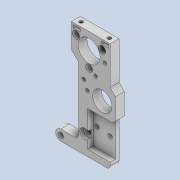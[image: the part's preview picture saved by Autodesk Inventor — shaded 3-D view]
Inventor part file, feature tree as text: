
AUTODESK INVENTOR PART (.ipt)
format: ipt  version: 2020.4 (Build 244396000, 396)  size: 391,168 bytes
history: native  units: mm
features: extrude x7, sketch x6, fillet x2, thread x2, projected_geometry x2
ambient origin geometry x8: Origin, YZ Plane, XZ Plane, XY Plane, X Axis, Y Axis, Z Axis, Center Point
bodies: Solid1 (feature_tree)
feature tree (19):
  extrude  "Extrusion1"  Depth=6.0mm
  fillet  "Fillet1"  Radius=28.0mm
  fillet  "Fillet2"  Radius=6.0mm
  extrude  "Extrusion2"  Depth=3.0mm
  extrude  "Extrusion3"  Depth=56.0mm
  thread  "Thread1"  [1 undecoded]
  thread  "Thread2"  [1 undecoded]
  extrude  "Extrusion4"  Depth=12.5mm
  extrude  "Extrusion5"  Depth=2.1mm
  extrude  "Extrusion6"  Depth=1.8mm TaperAngle=360.0deg
  extrude  "Extrusion7"  Depth=4.0mm
  sketch  "Sketch1"  dims[d0=3.0mm d1=6.0mm d2=28.0mm d3=6.0mm]
  sketch  "Sketch3"  dims[d4=0.0mm d5=3.0mm]
  projected_geometry  "Projected Loop1"
  sketch  "Sketch5"  dims[d6=18.0mm d7=56.0mm d8=11.0mm d9=4.5mm]
  sketch  "Sketch7"  dims[d10=25.5mm d11=12.5mm]
  sketch  "Sketch8"  dims[d12=22.3mm d14=2.1mm]
  projected_geometry  "Projected Loop2"
  sketch  "Sketch10"  dims[d17=9.5mm d18=30.0mm d20=360.0deg d22=4.0mm d23=14.0mm d24=45.0deg d25=3.0mm d26=12.0mm d27=6.0mm d28=135.0deg d29=135.0deg d30=5.0mm d31=0.0mm d32=3.0mm d33=10.5mm d34=3.5mm d35=2.5mm d36=14.5mm d37=7.5mm d38=2.5mm d39=15.0mm d40=13.5mm d41=2.0mm d42=2.0mm d43=12.75mm d44=20.0mm d45=23.75mm d46=3.0mm d47=0.0mm d48=2.0mm d49=2.0mm d50=2.5mm d51=2.5mm d52=3.0mm d53=3.0mm d54=3.0mm d55=0.0mm d56=7.0mm d57=0.0mm d58=7.0mm d59=0.0mm d60=8.5mm d61=270.0deg d62=4.0mm d63=4.0mm d64=4.0mm d65=3.0mm d66=0.0mm d67=5.5mm d68=2.0mm d69=0.0mm d70=4.0mm d71=1.85mm d72=4.0mm d73=1.85mm d74=1.0mm d75=1.8mm d76=1.8mm d77=1.0mm d78=10.0mm d79=0.0mm d82=2.0mm d83=11.15mm d84=2.1mm d85=2.1mm d86=2.1mm d87=5.0mm d88=3.0mm d89=25.0mm d90=29.5mm d91=3.0mm d92=11.0mm d93=24.0mm d94=8.0mm d95=2.1mm d96=2.1mm d98=2.1mm d99=1.8mm d100=0.0mm d101=2.1mm d102=2.1mm d80=0.5mm d81=0.872665mm d103=0.5mm d104=0.872665mm d105=0.5mm d106=0.872665mm]
note: 2 required parameter values undecoded (feature->parameter linkage not recoverable at this tier; creation-order binding heuristic only, values carry confidence <= 0.55)
